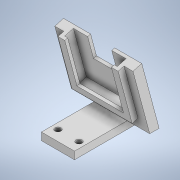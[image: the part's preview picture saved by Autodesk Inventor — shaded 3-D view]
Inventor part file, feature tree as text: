
AUTODESK INVENTOR PART (.ipt)
format: ipt  version: 2022 (Build 260153000, 153)  size: 238,592 bytes
history: native  units: mm
features: sketch x10, extrude x9, hole x1
ambient origin geometry x8: Origin, YZ Plane, XZ Plane, XY Plane, X Axis, Y Axis, Z Axis, Center Point
bodies: Solid1 (feature_tree)
feature tree (20):
  extrude  "Extrusion1"  Depth=35.0mm
  extrude  "Extrusion2"  TaperAngle=75.0deg  [1 undecoded]
  extrude  "Extrusion3"  Depth=22.0mm TaperAngle=0.0deg
  extrude  "Extrusion4"  Depth=15.0mm TaperAngle=0.0deg
  extrude  "Extrusion5"  Depth=15.0mm
  extrude  "Extrusion6"  Depth=15.0mm TaperAngle=0.0deg
  extrude  "Extrusion7"  Depth=31.404mm
  hole  "Hole1"  [1 undecoded]
  extrude  "Extrusion8"  Depth=40.0mm
  extrude  "Extrusion9"  Depth=4.0mm
  sketch  "Sketch1"  dims[d0=5.0mm d1=35.0mm]
  sketch  "Sketch2"  dims[d2=43.0mm d3=75.0deg]
  sketch  "Sketch3"  dims[d5=2.5mm d6=22.0mm d7=0.0mm]
  sketch  "Sketch4"  dims[d8=33.404mm d9=0.0mm d10=15.0mm d11=0.0mm]
  sketch  "Sketch5"  dims[d12=15.0mm d13=0.0mm d14=17.5mm]
  sketch  "Sketch6"  dims[d15=17.5mm d16=15.0mm d17=0.0mm]
  sketch  "Sketch7"  dims[d18=2.0mm d19=31.404mm]
  sketch  "Sketch8"  dims[d20=31.0mm d21=2.5mm]
  sketch  "Sketch9"  dims[d22=35.904mm d23=40.0mm]
  sketch  "Sketch10"  dims[d24=4.0mm d25=0.0mm d26=8.0mm d27=8.0mm d28=15.0mm d29=0.0mm d30=28.0mm d32=3.25mm d33=6.0mm d34=4.0mm d35=2.0mm d36=90.0deg d37=8.0mm d38=20.594885mm d39=1.0mm d40=0.0mm d41=4.0mm d42=0.0mm]
note: 2 required parameter values undecoded (feature->parameter linkage not recoverable at this tier; creation-order binding heuristic only, values carry confidence <= 0.55)
